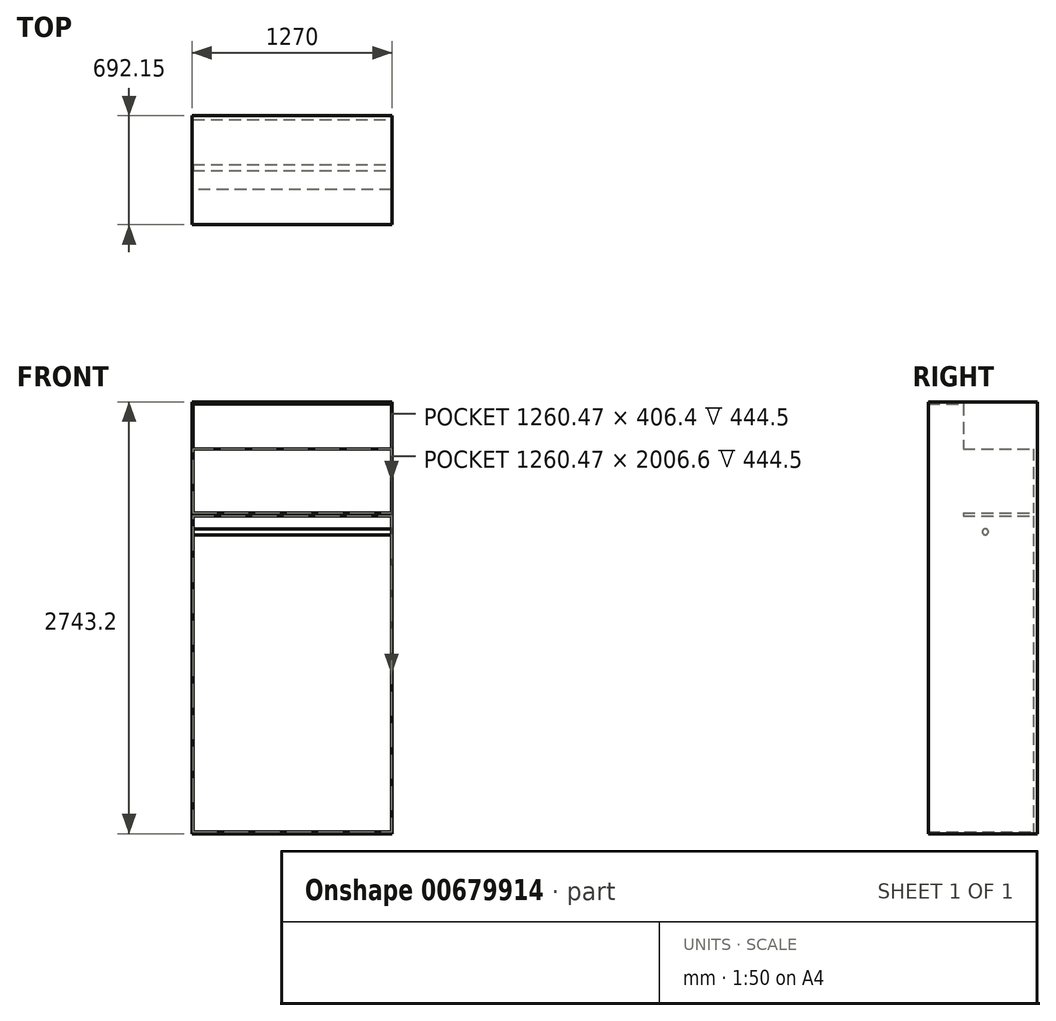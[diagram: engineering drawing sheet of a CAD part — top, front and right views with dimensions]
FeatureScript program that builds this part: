
annotation { "Feature Type Name" : "Feature", "Feature Type Description" : "" }
export const myFeature = defineFeature(function(context is Context, id is Id, definition is map)
    precondition{}
    {
        {
            var Q0;
            Q0=qCreatedBy(makeId("Front.planeOp"),FACE);
            var sketch = newSketch(context, id + "F0", { "sketchPlane" : qUnion([Q0])});
            skLineSegment(sketch, "E0.bottom", {"start": v(635, 1371.6) * mm, "end": v(-635, 1371.6) * mm});
            skLineSegment(sketch, "E0.top", {"start": v(635, -1371.6) * mm, "end": v(-635, -1371.6) * mm});
            skLineSegment(sketch, "E0.left", {"start": v(635, 1371.6) * mm, "end": v(635, -1371.6) * mm});
            skLineSegment(sketch, "E0.right", {"start": v(-635, 1371.6) * mm, "end": v(-635, -1371.6) * mm});
            skPoint(sketch, "E0.middle", {"position": v(0, 0) * mm});
            skSolve(sketch);
        }
        {
            var Q0;
            Q0 = qSketchRegion(id + "F0", true);
            extrude(context, id + "F1", {"entities" : qUnion([Q0]), "depth" : 25.4 * mm, "offsetDistance" : 25.4 * mm});
        }
        {
            var Q0;
            Q0=makeQuery(id+"F1.opExtrude","CAP_FACE",FACE,{"disambiguationData":[OSD([sQuery(id+"F0.wireOp",EDGE,"E0.bottom"),sQuery(id+"F0.wireOp",EDGE,"E0.top"),sQuery(id+"F0.wireOp",EDGE,"E0.left"),sQuery(id+"F0.wireOp",EDGE,"E0.right")])],"isStart":false});
            var sketch = newSketch(context, id + "F2", { "sketchPlane" : qUnion([Q0])});
            skLineSegment(sketch, "E1.bottom", {"start": v(630.24, 1358.9) * mm, "end": v(-630.24, 1358.9) * mm});
            skLineSegment(sketch, "E1.top", {"start": v(630.24, -1358.9) * mm, "end": v(-630.24, -1358.9) * mm});
            skLineSegment(sketch, "E1.left", {"start": v(630.24, 1358.9) * mm, "end": v(630.24, -1358.9) * mm});
            skLineSegment(sketch, "E1.right", {"start": v(-630.24, 1358.9) * mm, "end": v(-630.24, -1358.9) * mm});
            skPoint(sketch, "E1.middle", {"position": v(0, 0) * mm});
            skSolve(sketch);
        }
        {
            var Q0;
            Q0=makeQuery(id+"F2.imprint","IMPRINT",FACE,{"disambiguationData":[TD([[makeQuery(id+"F2.imprint","IMPRINT",EDGE,{"derivedFrom":sQuery(id+"F2.wireOp",EDGE,"E1.bottom")}),-1.0]])]});
            extrude(context, id + "F3", {"entities" : qUnion([Q0]), "operationType" : NewBodyOperationType.ADD, "depth" : 666.75 * mm, "offsetDistance" : 25.4 * mm});
        }
        {
            var Q0;
            Q0=makeQuery(id+"F1.opExtrude","CAP_FACE",FACE,{"disambiguationData":[OSD([sQuery(id+"F0.wireOp",EDGE,"E0.bottom"),sQuery(id+"F0.wireOp",EDGE,"E0.top"),sQuery(id+"F0.wireOp",EDGE,"E0.left"),sQuery(id+"F0.wireOp",EDGE,"E0.right")])],"isStart":false});
            var sketch = newSketch(context, id + "F4", { "sketchPlane" : qUnion([Q0])});
            skLineSegment(sketch, "E2", {"start": v(-630.24, 1073.15) * mm, "end": v(630.24, 1073.15) * mm});
            skLineSegment(sketch, "E3", {"start": v(-630.24, 666.75) * mm, "end": v(630.24, 666.75) * mm});
            skLineSegment(sketch, "E4", {"start": v(-630.24, 647.7) * mm, "end": v(630.24, 647.7) * mm});
            skSolve(sketch);
        }
        {
            var Q0;
            {var subQ0=sQuery(id+"F4.wireOp",EDGE,"E2");Q0=makeQuery(id+"F4.imprint","IMPRINT",FACE,{"disambiguationData":[TD([[makeQuery(id+"F4.imprint","IMPRINT",EDGE,{"derivedFrom":subQ0}),1.0]])]});}
            var Q1;
            {var subQ0=sQuery(id+"F4.wireOp",EDGE,"E3");Q1=makeQuery(id+"F4.imprint","IMPRINT",FACE,{"disambiguationData":[TD([[makeQuery(id+"F4.imprint","IMPRINT",EDGE,{"derivedFrom":subQ0}),-1.0]])]});}
            extrude(context, id + "F5", {"entities" : qUnion([Q0, Q1]), "operationType" : NewBodyOperationType.ADD, "depth" : 444.5 * mm, "offsetDistance" : 25.4 * mm});
        }
        {
            var Q0;
            Q0=makeQuery(id+"F3.opExtrude","SWEPT_FACE",FACE,{"disambiguationData":[OSD([sQuery(id+"F2.wireOp",EDGE,"E1.left")])]});
            var sketch = newSketch(context, id + "F6", { "sketchPlane" : qUnion([Q0])});
            skLineSegment(sketch, "E5", {"start": v(330.2, 647.7) * mm, "end": v(330.2, 307.17) * mm, "construction": true});
            skLineSegment(sketch, "E6", {"start": v(25.4, 546.1) * mm, "end": v(592.25, 546.1) * mm, "construction": true});
            skCircle(sketch, "E7", {"center": v(330.2, 546.1) * mm, "radius": 19.05 * mm});
            skSolve(sketch);
        }
        {
            var Q0;
            Q0=makeQuery(id+"F6.imprint","IMPRINT",FACE,{"disambiguationData":[TD([[makeQuery(id+"F6.imprint","IMPRINT",EDGE,{"derivedFrom":sQuery(id+"F6.wireOp",EDGE,"E7")}),1.0]])]});
            extrude(context, id + "F7", {"entities" : qUnion([Q0]), "endBound" : BoundingType.UP_TO_NEXT, "depth" : 25.4 * mm, "offsetDistance" : 25.4 * mm});
        }
    });
